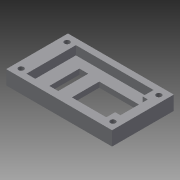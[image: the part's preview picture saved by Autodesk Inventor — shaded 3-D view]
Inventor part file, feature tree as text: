
AUTODESK INVENTOR PART (.ipt)
format: ipt  version: 2015 SP1 (Build 190203100, 203)  size: 144,896 bytes
history: native  units: mm
features: extrude x5, sketch x5, projected_geometry x4, hole x1, pattern_linear x1
ambient origin geometry x8: Origin, YZ Plane, XZ Plane, XY Plane, X Axis, Y Axis, Z Axis, Center Point
bodies: Solid1 (feature_tree)
feature tree (16):
  extrude  "Extrusion1"  Depth=30.0mm
  extrude  "Extrusion2"  Depth=15.5mm
  hole  "Hole1"  [1 undecoded]
  pattern_linear  "Rectangular Pattern1"  Spacing1=8.5mm  [1 undecoded]
  extrude  "Extrusion3"  Depth=7.0mm
  extrude  "Extrusion4"  Depth=3.0mm TaperAngle=0.0deg
  extrude  "Extrusion5"  Depth=44.0mm
  sketch  "Sketch1"  dims[d2=17.5mm d3=30.0mm]
  sketch  "Sketch2"  dims[d4=27.5mm d5=15.5mm]
  projected_geometry  "Projected Loop1"
  sketch  "Sketch3"  dims[d6=7.75mm d7=5.0mm]
  projected_geometry  "Projected Loop2"
  sketch  "Sketch4"  dims[d8=5.0mm]
  projected_geometry  "Projected Loop3"
  sketch  "Sketch5"  dims[d9=17.0mm d10=8.5mm d11=7.0mm d12=3.0mm d13=0.0mm d14=44.0mm d15=18.0mm d16=9.0mm d17=5.0mm d18=0.0mm d19=30.5mm d20=4.0mm d21=3.0mm d22=6.0mm d23=4.0mm d24=2.0mm d25=90.0deg d26=8.0mm d27=20.594885mm d28=20.0mm d30=52.0mm d31=20.0mm d33=26.0mm d34=5.0mm d35=0.0mm d36=5.0mm d37=0.0mm d38=5.0mm d39=0.0mm]
  projected_geometry  "Projected Loop4"
note: 2 required parameter values undecoded (feature->parameter linkage not recoverable at this tier; creation-order binding heuristic only, values carry confidence <= 0.55)
